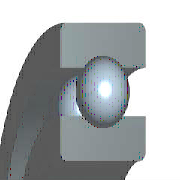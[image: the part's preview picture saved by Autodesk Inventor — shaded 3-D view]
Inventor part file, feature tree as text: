
AUTODESK INVENTOR PART (.ipt)
format: ipt  version: 2019 (Build 230136000, 136)  size: 355,840 bytes
history: native  units: mm (DEFAULTED — no unit token found)
features: other x3, plane x2, pattern_circular x1, sketch x1
ambient origin geometry x8: Origin, YZ Plane, XZ Plane, XY Plane, X Axis, Y Axis, Z Axis, Center Point
bodies: Solid1 (feature_tree)
feature tree (7):
  other  "WorkPoint1"
  other  "WorkAxis1"
  plane  "WorkPlane3"
  plane  "WorkPlane4"
  other  "WorkPoint2"
  pattern_circular  "Matriz polar1"  Count=2  [1 undecoded]
  sketch  "Boceto5"  dims[d1=6.0mm d2=72.0mm d3=19.0mm d4=19.0mm d5=6.0mm d6=360.0deg d7=0.0mm d8=15.6mm d9=3.9mm d10=360.0deg d11=-6.0mm d12=0.0mm d13=0.0mm d14=15.6001mm d15=3.9001mm d16=360.0deg d17=52.076923mm d19=360.0deg d20=0.3mm d21=5.08mm d22=6.25mm d23=7.42mm d26=0.0mm d27=0.0mm d28=0.0mm d29=0.0mm d30=0.0mm]
note: 1 required parameter value undecoded (feature->parameter linkage not recoverable at this tier; creation-order binding heuristic only, values carry confidence <= 0.55)
